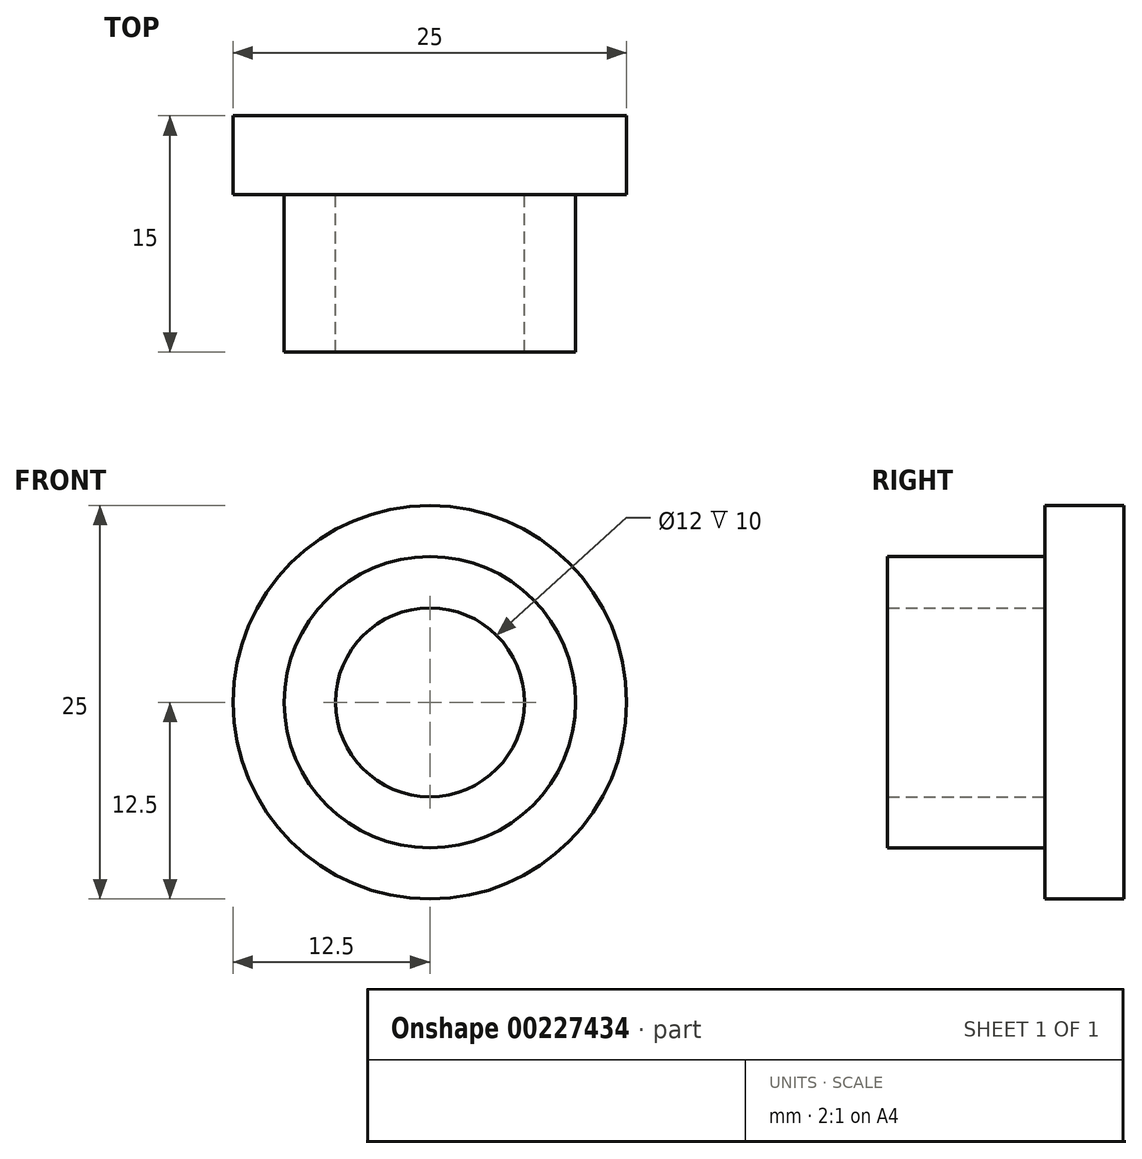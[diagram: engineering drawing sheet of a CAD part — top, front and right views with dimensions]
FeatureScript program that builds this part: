
annotation { "Feature Type Name" : "Feature", "Feature Type Description" : "" }
export const myFeature = defineFeature(function(context is Context, id is Id, definition is map)
    precondition{}
    {
        {
            var Q0;
            Q0=qCreatedBy(makeId("Front.planeOp"),FACE);
            var sketch = newSketch(context, id + "F0", { "sketchPlane" : qUnion([Q0])});
            skCircle(sketch, "E0", {"center": v(0, 0) * mm, "radius": 12.5 * mm});
            skSolve(sketch);
        }
        {
            var Q0;
            Q0 = qSketchRegion(id + "F0", true);
            extrude(context, id + "F1", {"entities" : qUnion([Q0]), "oppositeDirection" : true, "depth" : 5 * mm});
        }
        {
            var Q0;
            Q0=makeQuery(id+"F1.opExtrude","CAP_FACE",FACE,{"disambiguationData":[OSD([sQuery(id+"F0.wireOp",EDGE,"E0")])],"isStart":false});
            var sketch = newSketch(context, id + "F2", { "sketchPlane" : qUnion([Q0])});
            skCircle(sketch, "E1", {"center": v(0, 0) * mm, "radius": 9.25 * mm});
            skCircle(sketch, "E2", {"center": v(0, 0) * mm, "radius": 6 * mm});
            skSolve(sketch);
        }
        {
            var Q0;
            Q0 = qSketchRegion(id + "F2", true);
            extrude(context, id + "F3", {"entities" : qUnion([Q0]), "operationType" : NewBodyOperationType.ADD, "oppositeDirection" : true, "depth" : 15 * mm});
        }
    });
